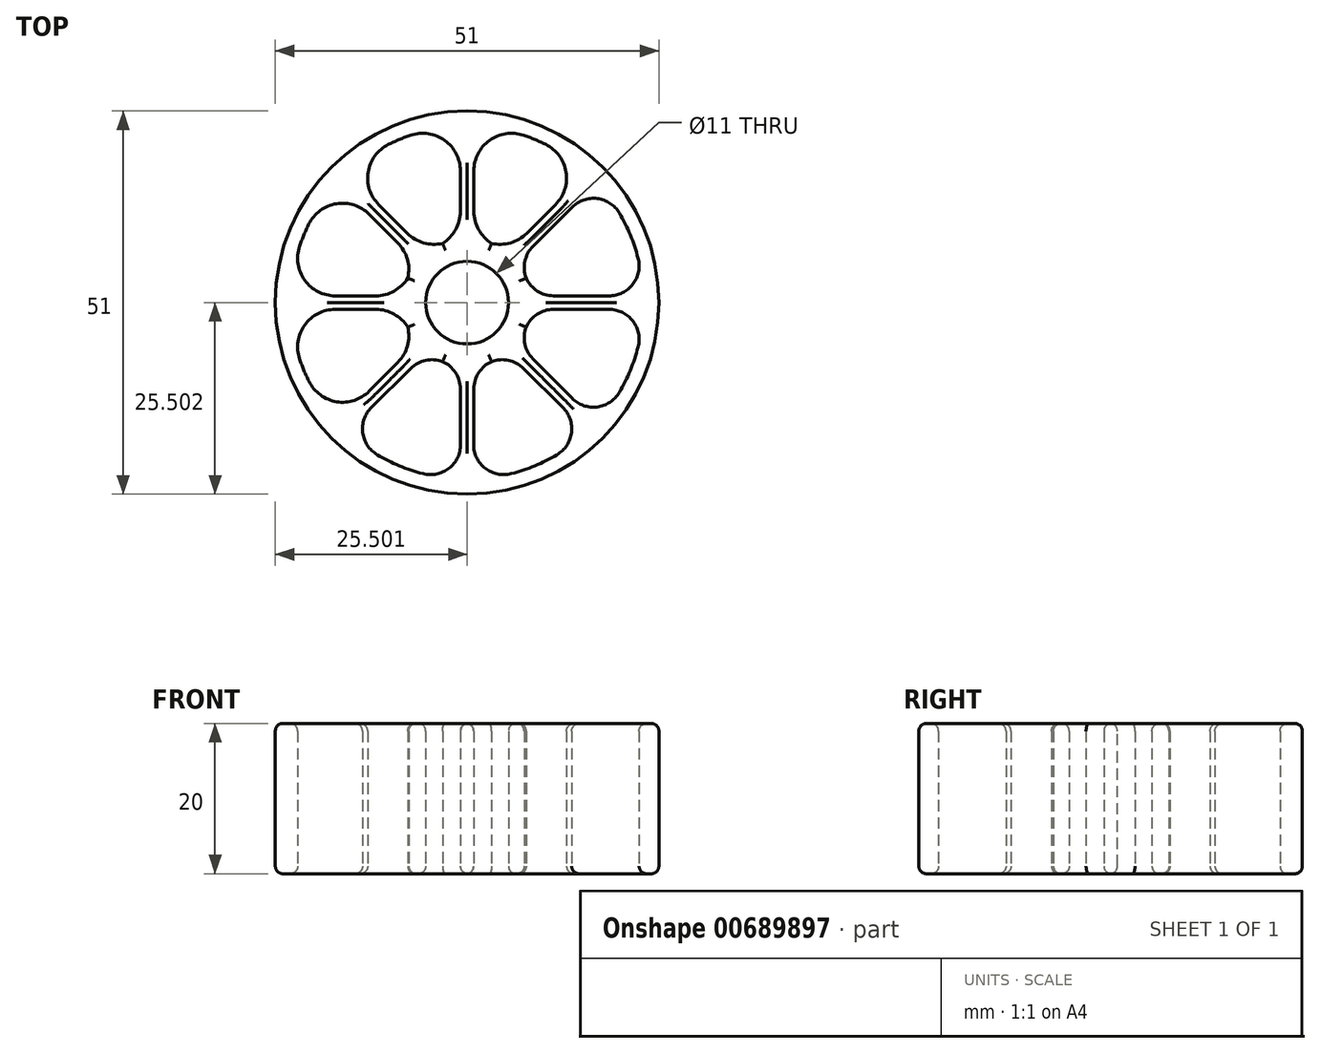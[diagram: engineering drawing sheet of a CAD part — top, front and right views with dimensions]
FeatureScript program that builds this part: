
annotation { "Feature Type Name" : "Feature", "Feature Type Description" : "" }
export const myFeature = defineFeature(function(context is Context, id is Id, definition is map)
    precondition{}
    {
        {
            var Q0;
            Q0=qCreatedBy(makeId("Top.planeOp"),FACE);
            var sketch = newSketch(context, id + "F0", { "sketchPlane" : qUnion([Q0])});
            skCircle(sketch, "E0", {"center": v(0.08, 0.1) * mm, "radius": 5.5 * mm});
            skArc(sketch, "E1", {"start": v(5.42, 6.7) * mm, "mid": v(3.33, 7.95) * mm, "end": v(0.98, 8.54) * mm});
            skCircle(sketch, "E2", {"center": v(0.08, 0.1) * mm, "radius": 25.5 * mm});
            skArc(sketch, "E3", {"start": v(-0.82, 23.58) * mm, "mid": v(-8.91, 21.8) * mm, "end": v(-15.89, 17.33) * mm});
            skLineSegment(sketch, "E4.left", {"start": v(16.05, 17.33) * mm, "end": v(5.42, 6.7) * mm});
            skLineSegment(sketch, "E4.right", {"start": v(17.32, 16.06) * mm, "end": v(6.7, 5.43) * mm});
            skLineSegment(sketch, "E5.bottom", {"start": v(-15.89, 17.33) * mm, "end": v(-5.26, 6.7) * mm});
            skLineSegment(sketch, "E5.top", {"start": v(-17.16, 16.06) * mm, "end": v(-6.53, 5.43) * mm});
            skLineSegment(sketch, "E6.left", {"start": v(-0.82, 23.58) * mm, "end": v(-0.82, 8.54) * mm});
            skLineSegment(sketch, "E6.right", {"start": v(0.98, 23.58) * mm, "end": v(0.98, 8.54) * mm});
            skLineSegment(sketch, "E7.bottom", {"start": v(-23.4, 1) * mm, "end": v(-8.37, 1) * mm});
            skLineSegment(sketch, "E7.top", {"start": v(-23.4, -0.8) * mm, "end": v(-8.37, -0.8) * mm});
            skLineSegment(sketch, "E8.trimOffspring", {"start": v(8.53, 1) * mm, "end": v(23.56, 1) * mm});
            skLineSegment(sketch, "E9.trimOffspring", {"start": v(8.53, -0.8) * mm, "end": v(23.56, -0.8) * mm});
            skLineSegment(sketch, "E10.trimOffspring", {"start": v(-6.53, -5.25) * mm, "end": v(-17.12, -15.92) * mm});
            skLineSegment(sketch, "E11.trimOffspring", {"start": v(-5.26, -6.52) * mm, "end": v(-15.93, -17.11) * mm});
            skLineSegment(sketch, "E12.trimOffspring", {"start": v(-0.82, -8.36) * mm, "end": v(-0.77, -23.4) * mm});
            skLineSegment(sketch, "E13.trimOffspring", {"start": v(0.98, -8.36) * mm, "end": v(0.93, -23.4) * mm});
            skLineSegment(sketch, "E14.trimOffspring", {"start": v(5.42, -6.52) * mm, "end": v(16.09, -17.11) * mm});
            skLineSegment(sketch, "E15.trimOffspring", {"start": v(6.7, -5.25) * mm, "end": v(17.28, -15.92) * mm});
            skArc(sketch, "E16.trimOffspring", {"start": v(-17.16, 16.06) * mm, "mid": v(-21.63, 9.09) * mm, "end": v(-23.4, 1) * mm});
            skArc(sketch, "E17.trimOffspring", {"start": v(-23.4, -0.8) * mm, "mid": v(-21.62, -8.93) * mm, "end": v(-17.12, -15.92) * mm});
            skArc(sketch, "E18.trimOffspring", {"start": v(-15.93, -17.11) * mm, "mid": v(-8.91, -21.62) * mm, "end": v(-0.77, -23.4) * mm});
            skArc(sketch, "E19.trimOffspring", {"start": v(0.93, -23.4) * mm, "mid": v(9.07, -21.62) * mm, "end": v(16.09, -17.11) * mm});
            skArc(sketch, "E20.trimOffspring", {"start": v(17.28, -15.92) * mm, "mid": v(21.78, -8.93) * mm, "end": v(23.56, -0.8) * mm});
            skArc(sketch, "E21.trimOffspring", {"start": v(23.56, 1) * mm, "mid": v(21.8, 9.09) * mm, "end": v(17.32, 16.06) * mm});
            skArc(sketch, "E22.trimOffspring", {"start": v(16.05, 17.33) * mm, "mid": v(9.07, 21.8) * mm, "end": v(0.98, 23.58) * mm});
            skArc(sketch, "E23.trimOffspring", {"start": v(8.53, 1) * mm, "mid": v(7.93, 3.35) * mm, "end": v(6.7, 5.43) * mm});
            skArc(sketch, "E24.trimOffspring", {"start": v(6.7, -5.25) * mm, "mid": v(7.93, -3.16) * mm, "end": v(8.53, -0.8) * mm});
            skArc(sketch, "E25.trimOffspring", {"start": v(0.98, -8.36) * mm, "mid": v(3.33, -7.76) * mm, "end": v(5.42, -6.52) * mm});
            skArc(sketch, "E26.trimOffspring", {"start": v(-5.26, -6.52) * mm, "mid": v(-3.17, -7.76) * mm, "end": v(-0.82, -8.36) * mm});
            skArc(sketch, "E27.trimOffspring", {"start": v(-8.37, -0.8) * mm, "mid": v(-7.77, -3.16) * mm, "end": v(-6.53, -5.25) * mm});
            skArc(sketch, "E28.trimOffspring", {"start": v(-6.53, 5.43) * mm, "mid": v(-7.77, 3.35) * mm, "end": v(-8.37, 1) * mm});
            skArc(sketch, "E29.trimOffspring", {"start": v(-0.82, 8.54) * mm, "mid": v(-3.17, 7.95) * mm, "end": v(-5.26, 6.7) * mm});
            skSolve(sketch);
        }
        {
            var Q0;
            Q0=makeQuery(id+"F0.imprint","IMPRINT",FACE,{"disambiguationData":[TD([[makeQuery(id+"F0.imprint","IMPRINT",EDGE,{"derivedFrom":sQuery(id+"F0.wireOp",EDGE,"E2")}),1.0]])]});
            var Q1;
            {var subQ0=sQuery(id+"F0.wireOp",EDGE,"E7.bottom");Q1=makeQuery(id+"F0.imprint","IMPRINT",FACE,{"disambiguationData":[TD([[makeQuery(id+"F0.imprint","IMPRINT",EDGE,{"derivedFrom":subQ0}),-1.0]])]});}
            var Q2;
            {var subQ0=sQuery(id+"F0.wireOp",EDGE,"E5.bottom");Q2=makeQuery(id+"F0.imprint","IMPRINT",FACE,{"disambiguationData":[TD([[makeQuery(id+"F0.imprint","IMPRINT",EDGE,{"derivedFrom":subQ0}),-1.0]])]});}
            var Q3;
            Q3=makeQuery(id+"F0.imprint","IMPRINT",FACE,{"disambiguationData":[TD([[makeQuery(id+"F0.imprint","IMPRINT",EDGE,{"derivedFrom":sQuery(id+"F0.wireOp",EDGE,"E6.bottom")}),-1.0]])]});
            var Q4;
            Q4=makeQuery(id+"F0.imprint","IMPRINT",FACE,{"disambiguationData":[TD([[makeQuery(id+"F0.imprint","IMPRINT",EDGE,{"derivedFrom":sQuery(id+"F0.wireOp",EDGE,"E4.bottom")}),-1.0]])]});
            var Q5;
            Q5=makeQuery(id+"F0.imprint","IMPRINT",FACE,{"disambiguationData":[TD([[makeQuery(id+"F0.imprint","IMPRINT",EDGE,{"derivedFrom":sQuery(id+"F0.wireOp",EDGE,"E7.right")}),-1.0]])]});
            var Q6;
            Q6=makeQuery(id+"F0.imprint","IMPRINT",FACE,{"disambiguationData":[TD([[makeQuery(id+"F0.imprint","IMPRINT",EDGE,{"derivedFrom":sQuery(id+"F0.wireOp",EDGE,"E0")}),-1.0]])]});
            var Q7;
            Q7=makeQuery(id+"F0.imprint","IMPRINT",FACE,{"disambiguationData":[TD([[makeQuery(id+"F0.imprint","IMPRINT",EDGE,{"derivedFrom":sQuery(id+"F0.wireOp",EDGE,"E5.right")}),-1.0]])]});
            var Q8;
            Q8=makeQuery(id+"F0.imprint","IMPRINT",FACE,{"disambiguationData":[TD([[makeQuery(id+"F0.imprint","IMPRINT",EDGE,{"derivedFrom":sQuery(id+"F0.wireOp",EDGE,"E6.top")}),1.0]])]});
            var Q9;
            Q9=makeQuery(id+"F0.imprint","IMPRINT",FACE,{"disambiguationData":[TD([[makeQuery(id+"F0.imprint","IMPRINT",EDGE,{"derivedFrom":sQuery(id+"F0.wireOp",EDGE,"E4.top")}),1.0]])]});
            extrude(context, id + "F1", {"entities" : qUnion([Q0, Q1, Q2, Q3, Q4, Q5, Q6, Q7, Q8, Q9]), "depth" : 20 * mm, "offsetDistance" : 25 * mm});
        }
        {
            var Q0;
            Q0=makeQuery(id+"F1.opExtrude","SWEPT_EDGE",EDGE,{"disambiguationData":[OSD([sQuery(id+"F0.wireOp",EDGE,"E14.trimOffspring"),sQuery(id+"F0.wireOp",EDGE,"E25.trimOffspring")])]});
            var Q1;
            Q1=makeQuery(id+"F1.opExtrude","SWEPT_EDGE",EDGE,{"disambiguationData":[OSD([sQuery(id+"F0.wireOp",EDGE,"E13.trimOffspring"),sQuery(id+"F0.wireOp",EDGE,"E25.trimOffspring")])]});
            var Q2;
            Q2=makeQuery(id+"F1.opExtrude","SWEPT_EDGE",EDGE,{"disambiguationData":[OSD([sQuery(id+"F0.wireOp",EDGE,"E13.trimOffspring"),sQuery(id+"F0.wireOp",EDGE,"E19.trimOffspring")])]});
            var Q3;
            Q3=makeQuery(id+"F1.opExtrude","SWEPT_EDGE",EDGE,{"disambiguationData":[OSD([sQuery(id+"F0.wireOp",EDGE,"E14.trimOffspring"),sQuery(id+"F0.wireOp",EDGE,"E19.trimOffspring")])]});
            var Q4;
            Q4=makeQuery(id+"F1.opExtrude","SWEPT_EDGE",EDGE,{"disambiguationData":[OSD([sQuery(id+"F0.wireOp",EDGE,"E12.trimOffspring"),sQuery(id+"F0.wireOp",EDGE,"E26.trimOffspring")])]});
            var Q5;
            Q5=makeQuery(id+"F1.opExtrude","SWEPT_EDGE",EDGE,{"disambiguationData":[OSD([sQuery(id+"F0.wireOp",EDGE,"E11.trimOffspring"),sQuery(id+"F0.wireOp",EDGE,"E26.trimOffspring")])]});
            var Q6;
            Q6=makeQuery(id+"F1.opExtrude","SWEPT_EDGE",EDGE,{"disambiguationData":[OSD([sQuery(id+"F0.wireOp",EDGE,"E11.trimOffspring"),sQuery(id+"F0.wireOp",EDGE,"E18.trimOffspring")])]});
            var Q7;
            Q7=makeQuery(id+"F1.opExtrude","SWEPT_EDGE",EDGE,{"disambiguationData":[OSD([sQuery(id+"F0.wireOp",EDGE,"E12.trimOffspring"),sQuery(id+"F0.wireOp",EDGE,"E18.trimOffspring")])]});
            var Q8;
            Q8=makeQuery(id+"F1.opExtrude","SWEPT_EDGE",EDGE,{"disambiguationData":[OSD([sQuery(id+"F0.wireOp",EDGE,"E9.trimOffspring"),sQuery(id+"F0.wireOp",EDGE,"E24.trimOffspring")])]});
            var Q9;
            Q9=makeQuery(id+"F1.opExtrude","SWEPT_EDGE",EDGE,{"disambiguationData":[OSD([sQuery(id+"F0.wireOp",EDGE,"E15.trimOffspring"),sQuery(id+"F0.wireOp",EDGE,"E24.trimOffspring")])]});
            var Q10;
            Q10=makeQuery(id+"F1.opExtrude","SWEPT_EDGE",EDGE,{"disambiguationData":[OSD([sQuery(id+"F0.wireOp",EDGE,"E15.trimOffspring"),sQuery(id+"F0.wireOp",EDGE,"E20.trimOffspring")])]});
            var Q11;
            Q11=makeQuery(id+"F1.opExtrude","SWEPT_EDGE",EDGE,{"disambiguationData":[OSD([sQuery(id+"F0.wireOp",EDGE,"E9.trimOffspring"),sQuery(id+"F0.wireOp",EDGE,"E20.trimOffspring")])]});
            var Q12;
            Q12=makeQuery(id+"F1.opExtrude","SWEPT_EDGE",EDGE,{"disambiguationData":[OSD([sQuery(id+"F0.wireOp",EDGE,"E4.right"),sQuery(id+"F0.wireOp",EDGE,"E23.trimOffspring")])]});
            var Q13;
            Q13=makeQuery(id+"F1.opExtrude","SWEPT_EDGE",EDGE,{"disambiguationData":[OSD([sQuery(id+"F0.wireOp",EDGE,"E8.trimOffspring"),sQuery(id+"F0.wireOp",EDGE,"E23.trimOffspring")])]});
            var Q14;
            Q14=makeQuery(id+"F1.opExtrude","SWEPT_EDGE",EDGE,{"disambiguationData":[OSD([sQuery(id+"F0.wireOp",EDGE,"E4.right"),sQuery(id+"F0.wireOp",EDGE,"E21.trimOffspring")])]});
            var Q15;
            Q15=makeQuery(id+"F1.opExtrude","SWEPT_EDGE",EDGE,{"disambiguationData":[OSD([sQuery(id+"F0.wireOp",EDGE,"E8.trimOffspring"),sQuery(id+"F0.wireOp",EDGE,"E21.trimOffspring")])]});
            fillet(context, id + "F2", {"entities" : qUnion([Q0, Q1, Q2, Q3, Q4, Q5, Q6, Q7, Q8, Q9, Q10, Q11, Q12, Q13, Q14, Q15]), "radius" : 4 * mm, "tangentPropagation" : true, "allowEdgeOverflow" : false});
        }
        {
            var Q0;
            Q0=makeQuery(id+"F1.opExtrude","SWEPT_EDGE",EDGE,{"disambiguationData":[OSD([sQuery(id+"F0.wireOp",EDGE,"E7.top"),sQuery(id+"F0.wireOp",EDGE,"E17.trimOffspring")])]});
            var Q1;
            Q1=makeQuery(id+"F1.opExtrude","SWEPT_EDGE",EDGE,{"disambiguationData":[OSD([sQuery(id+"F0.wireOp",EDGE,"E7.top"),sQuery(id+"F0.wireOp",EDGE,"E27.trimOffspring")])]});
            var Q2;
            Q2=makeQuery(id+"F1.opExtrude","SWEPT_EDGE",EDGE,{"disambiguationData":[OSD([sQuery(id+"F0.wireOp",EDGE,"E10.trimOffspring"),sQuery(id+"F0.wireOp",EDGE,"E27.trimOffspring")])]});
            var Q3;
            Q3=makeQuery(id+"F1.opExtrude","SWEPT_EDGE",EDGE,{"disambiguationData":[OSD([sQuery(id+"F0.wireOp",EDGE,"E10.trimOffspring"),sQuery(id+"F0.wireOp",EDGE,"E17.trimOffspring")])]});
            var Q4;
            Q4=makeQuery(id+"F1.opExtrude","SWEPT_EDGE",EDGE,{"disambiguationData":[OSD([sQuery(id+"F0.wireOp",EDGE,"E5.top"),sQuery(id+"F0.wireOp",EDGE,"E16.trimOffspring")])]});
            var Q5;
            Q5=makeQuery(id+"F1.opExtrude","SWEPT_EDGE",EDGE,{"disambiguationData":[OSD([sQuery(id+"F0.wireOp",EDGE,"E7.bottom"),sQuery(id+"F0.wireOp",EDGE,"E28.trimOffspring")])]});
            var Q6;
            Q6=makeQuery(id+"F1.opExtrude","SWEPT_EDGE",EDGE,{"disambiguationData":[OSD([sQuery(id+"F0.wireOp",EDGE,"E5.top"),sQuery(id+"F0.wireOp",EDGE,"E28.trimOffspring")])]});
            var Q7;
            Q7=makeQuery(id+"F1.opExtrude","SWEPT_EDGE",EDGE,{"disambiguationData":[OSD([sQuery(id+"F0.wireOp",EDGE,"E7.bottom"),sQuery(id+"F0.wireOp",EDGE,"E16.trimOffspring")])]});
            var Q8;
            Q8=makeQuery(id+"F1.opExtrude","SWEPT_EDGE",EDGE,{"disambiguationData":[OSD([sQuery(id+"F0.wireOp",EDGE,"E3"),sQuery(id+"F0.wireOp",EDGE,"E5.bottom")])]});
            var Q9;
            Q9=makeQuery(id+"F1.opExtrude","SWEPT_EDGE",EDGE,{"disambiguationData":[OSD([sQuery(id+"F0.wireOp",EDGE,"E5.bottom"),sQuery(id+"F0.wireOp",EDGE,"E29.trimOffspring")])]});
            var Q10;
            Q10=makeQuery(id+"F1.opExtrude","SWEPT_EDGE",EDGE,{"disambiguationData":[OSD([sQuery(id+"F0.wireOp",EDGE,"E6.left"),sQuery(id+"F0.wireOp",EDGE,"E29.trimOffspring")])]});
            var Q11;
            Q11=makeQuery(id+"F1.opExtrude","SWEPT_EDGE",EDGE,{"disambiguationData":[OSD([sQuery(id+"F0.wireOp",EDGE,"E1"),sQuery(id+"F0.wireOp",EDGE,"E4.left")])]});
            var Q12;
            Q12=makeQuery(id+"F1.opExtrude","SWEPT_EDGE",EDGE,{"disambiguationData":[OSD([sQuery(id+"F0.wireOp",EDGE,"E1"),sQuery(id+"F0.wireOp",EDGE,"E6.right")])]});
            var Q13;
            Q13=makeQuery(id+"F1.opExtrude","SWEPT_EDGE",EDGE,{"disambiguationData":[OSD([sQuery(id+"F0.wireOp",EDGE,"E3"),sQuery(id+"F0.wireOp",EDGE,"E6.left")])]});
            var Q14;
            Q14=makeQuery(id+"F1.opExtrude","SWEPT_EDGE",EDGE,{"disambiguationData":[OSD([sQuery(id+"F0.wireOp",EDGE,"E6.right"),sQuery(id+"F0.wireOp",EDGE,"E22.trimOffspring")])]});
            var Q15;
            Q15=makeQuery(id+"F1.opExtrude","SWEPT_EDGE",EDGE,{"disambiguationData":[OSD([sQuery(id+"F0.wireOp",EDGE,"E4.left"),sQuery(id+"F0.wireOp",EDGE,"E22.trimOffspring")])]});
            fillet(context, id + "F3", {"entities" : qUnion([Q0, Q1, Q2, Q3, Q4, Q5, Q6, Q7, Q8, Q9, Q10, Q11, Q12, Q13, Q14, Q15]), "radius" : 5 * mm, "tangentPropagation" : true, "allowEdgeOverflow" : false});
        }
        {
            var Q0;
            Q0=makeQuery(id+"F1.opExtrude","CAP_FACE",FACE,{"disambiguationData":[OSD([sQuery(id+"F0.wireOp",EDGE,"E0"),sQuery(id+"F0.wireOp",EDGE,"E1"),sQuery(id+"F0.wireOp",EDGE,"E2"),sQuery(id+"F0.wireOp",EDGE,"E3"),sQuery(id+"F0.wireOp",EDGE,"E4.left"),sQuery(id+"F0.wireOp",EDGE,"E4.right"),sQuery(id+"F0.wireOp",EDGE,"E5.bottom"),sQuery(id+"F0.wireOp",EDGE,"E5.top"),sQuery(id+"F0.wireOp",EDGE,"E6.left"),sQuery(id+"F0.wireOp",EDGE,"E6.right"),sQuery(id+"F0.wireOp",EDGE,"E7.bottom"),sQuery(id+"F0.wireOp",EDGE,"E7.top"),sQuery(id+"F0.wireOp",EDGE,"E8.trimOffspring"),sQuery(id+"F0.wireOp",EDGE,"E9.trimOffspring"),sQuery(id+"F0.wireOp",EDGE,"E10.trimOffspring"),sQuery(id+"F0.wireOp",EDGE,"E11.trimOffspring"),sQuery(id+"F0.wireOp",EDGE,"E12.trimOffspring"),sQuery(id+"F0.wireOp",EDGE,"E13.trimOffspring"),sQuery(id+"F0.wireOp",EDGE,"E14.trimOffspring"),sQuery(id+"F0.wireOp",EDGE,"E15.trimOffspring"),sQuery(id+"F0.wireOp",EDGE,"E16.trimOffspring"),sQuery(id+"F0.wireOp",EDGE,"E17.trimOffspring"),sQuery(id+"F0.wireOp",EDGE,"E18.trimOffspring"),sQuery(id+"F0.wireOp",EDGE,"E19.trimOffspring"),sQuery(id+"F0.wireOp",EDGE,"E20.trimOffspring"),sQuery(id+"F0.wireOp",EDGE,"E21.trimOffspring"),sQuery(id+"F0.wireOp",EDGE,"E22.trimOffspring"),sQuery(id+"F0.wireOp",EDGE,"E23.trimOffspring"),sQuery(id+"F0.wireOp",EDGE,"E24.trimOffspring"),sQuery(id+"F0.wireOp",EDGE,"E25.trimOffspring"),sQuery(id+"F0.wireOp",EDGE,"E26.trimOffspring"),sQuery(id+"F0.wireOp",EDGE,"E27.trimOffspring"),sQuery(id+"F0.wireOp",EDGE,"E28.trimOffspring"),sQuery(id+"F0.wireOp",EDGE,"E29.trimOffspring")])],"isStart":false});
            var Q1;
            Q1=makeQuery(id+"F1.opExtrude","CAP_FACE",FACE,{"disambiguationData":[OSD([sQuery(id+"F0.wireOp",EDGE,"E0"),sQuery(id+"F0.wireOp",EDGE,"E1"),sQuery(id+"F0.wireOp",EDGE,"E2"),sQuery(id+"F0.wireOp",EDGE,"E3"),sQuery(id+"F0.wireOp",EDGE,"E4.left"),sQuery(id+"F0.wireOp",EDGE,"E4.right"),sQuery(id+"F0.wireOp",EDGE,"E5.bottom"),sQuery(id+"F0.wireOp",EDGE,"E5.top"),sQuery(id+"F0.wireOp",EDGE,"E6.left"),sQuery(id+"F0.wireOp",EDGE,"E6.right"),sQuery(id+"F0.wireOp",EDGE,"E7.bottom"),sQuery(id+"F0.wireOp",EDGE,"E7.top"),sQuery(id+"F0.wireOp",EDGE,"E8.trimOffspring"),sQuery(id+"F0.wireOp",EDGE,"E9.trimOffspring"),sQuery(id+"F0.wireOp",EDGE,"E10.trimOffspring"),sQuery(id+"F0.wireOp",EDGE,"E11.trimOffspring"),sQuery(id+"F0.wireOp",EDGE,"E12.trimOffspring"),sQuery(id+"F0.wireOp",EDGE,"E13.trimOffspring"),sQuery(id+"F0.wireOp",EDGE,"E14.trimOffspring"),sQuery(id+"F0.wireOp",EDGE,"E15.trimOffspring"),sQuery(id+"F0.wireOp",EDGE,"E16.trimOffspring"),sQuery(id+"F0.wireOp",EDGE,"E17.trimOffspring"),sQuery(id+"F0.wireOp",EDGE,"E18.trimOffspring"),sQuery(id+"F0.wireOp",EDGE,"E19.trimOffspring"),sQuery(id+"F0.wireOp",EDGE,"E20.trimOffspring"),sQuery(id+"F0.wireOp",EDGE,"E21.trimOffspring"),sQuery(id+"F0.wireOp",EDGE,"E22.trimOffspring"),sQuery(id+"F0.wireOp",EDGE,"E23.trimOffspring"),sQuery(id+"F0.wireOp",EDGE,"E24.trimOffspring"),sQuery(id+"F0.wireOp",EDGE,"E25.trimOffspring"),sQuery(id+"F0.wireOp",EDGE,"E26.trimOffspring"),sQuery(id+"F0.wireOp",EDGE,"E27.trimOffspring"),sQuery(id+"F0.wireOp",EDGE,"E28.trimOffspring"),sQuery(id+"F0.wireOp",EDGE,"E29.trimOffspring")])],"isStart":true});
            fillet(context, id + "F4", {"entities" : qUnion([Q0, Q1]), "radius" : 1 * mm, "tangentPropagation" : true, "allowEdgeOverflow" : false});
        }
    });
